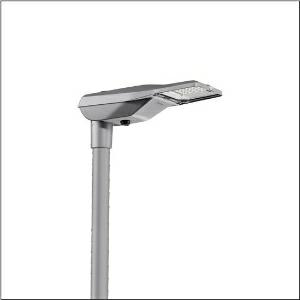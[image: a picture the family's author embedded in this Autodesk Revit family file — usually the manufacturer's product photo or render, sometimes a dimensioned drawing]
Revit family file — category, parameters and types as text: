
# Revit family: streetlight_sl_21_iq_micro___st1_0ab_5xe1m31u08db_013b
name_source: partatom
category: Lighting Fixtures
units: mm (PartAtom-declared; Revit-internal decimal feet)

## family parameters
Cut with Voids When Loaded = No
Host = Face
Light Source = No
Part Type = Normal
Room Calculation Point = No
Round Connector Dimension = Use Diameter
Shared = No

## types (1)
- --- (1 x LED, 4490 lm, 39.1 W, 3000K)
    Apparent Load = 39 VA
    CIE Flux Codes = 38 73 97 100 100
    Color Rendering = 70
    Color Temperature = 3000K
    Default Elevation = 1800 mm
    Description = Streetlight SL 21 iQ micro, mast luminaire, primary light control with lens, of PMMA, primary optical cover: cover, of toughened safety glass, transparent, light distribution: ST1.0aB, light emission: direct distribution, primary light characteristic: asymmetric, installation type: post-top, side-entry, LED, High Power LED, rated luminous flux: 4.490lm, luminous efficacy: 115lm/W, light colour: 730, colour temperature: 3000K, control gear: iQ-Street Remote, D4i with power reduction, control: pre-setting: logarithmic dimming characteristic, Street-Remote, Auto-Match, Temp-Guard, Lumen-Switch, Night-Set, Smart-Wire, Light-Fading, Desk-Remote (wireless, voltage-free reading and setting of iQ features in the workshop via application-optimized NFC function/RFID function), optimised constant luminous flux control (CLO 2.0), mains connection: 220..240V, AC, 50/60Hz, start of lifetime: 39W, end of service life: 41W, reduction: 17W, luminaire housing, of diecast aluminium, powder-coated, Siteco® metallic grey (DB 702S), corrosivity category C5 mid according to DIN EN ISO 12944, please order mast flange separately, inclination adjustable: 0°, 5°, 10°, 15°, sealing non-destructively replaceable, multi-level sealing system, length: 528mm, width: 235mm, height: 110mm, mast flange for spigot size: 42mm (side-entry): 5XC10008XM4, 60/48mm (side-entry/post-top): 5XC10108XM2, 76/60mm (side-entry/post-top): 5XC10108XM1, mounting height: 4..8m, Smart Interface below, protection rating (complete): IP66, insulation class (complete): insulation class II (safety insulation), certification: CE, ENEC, ENEC+, VDE, impact resistance: IK10, permissible operating ambient temperature for outdoor applications: -40..+50°C, standard-compliant lighting for roads and squares, packaging unit: 1 piece

Light Distribution: ST1.0aB
    Height = 110 mm
    Lamp = 1 x LED
    Lamp Light Flux = 4490 lm
    Lamp Power = 39.1 W
    Lamp count = 1
    Length = 528 mm
    Luminous efficacy = 115 lm/W
    Manufacturer = Siteco
    ModVariant = No
    Model = 5XE1M31U08DB
    Number of Poles = 1
    OnlyDefault = Yes
    Power Factor = 1
    Product Name = Streetlight SL 21 iQ micro | ST1.0aB
    Product group = mast luminaire | pylon top
    ProductGroupID = 6100
    Protection Class = Protection class II
    Protection Degree = IP 66
    RLX_Detail_Level = 1
    RLX_Emergency_Light_Flux = 0 lm
    RLX_Emergency_Type = 0
    RLX_Emergency_Type_DB = No
    RlxData = <blob elided: 99057 chars, md5=f138b58b>
    Socket = socket
    Standby Power = 0 W
    System Light Flux = 4490 lm
    System Power = 39 W
    Type Comments = factory setting: luminous flux: 100 % | dim-lin: 254 | 765 mA
    Type Image = l_1277290.jpg
    URL = http://relux.com
    VarID = @adj_134263
    Voltage = 0 V
    Weight = 0.00 kg
    Width = 235 mm

## geometry (parser evidence)
native form markers: Blend x4, Sweep x9
no freeform markers — native parametric forms only
